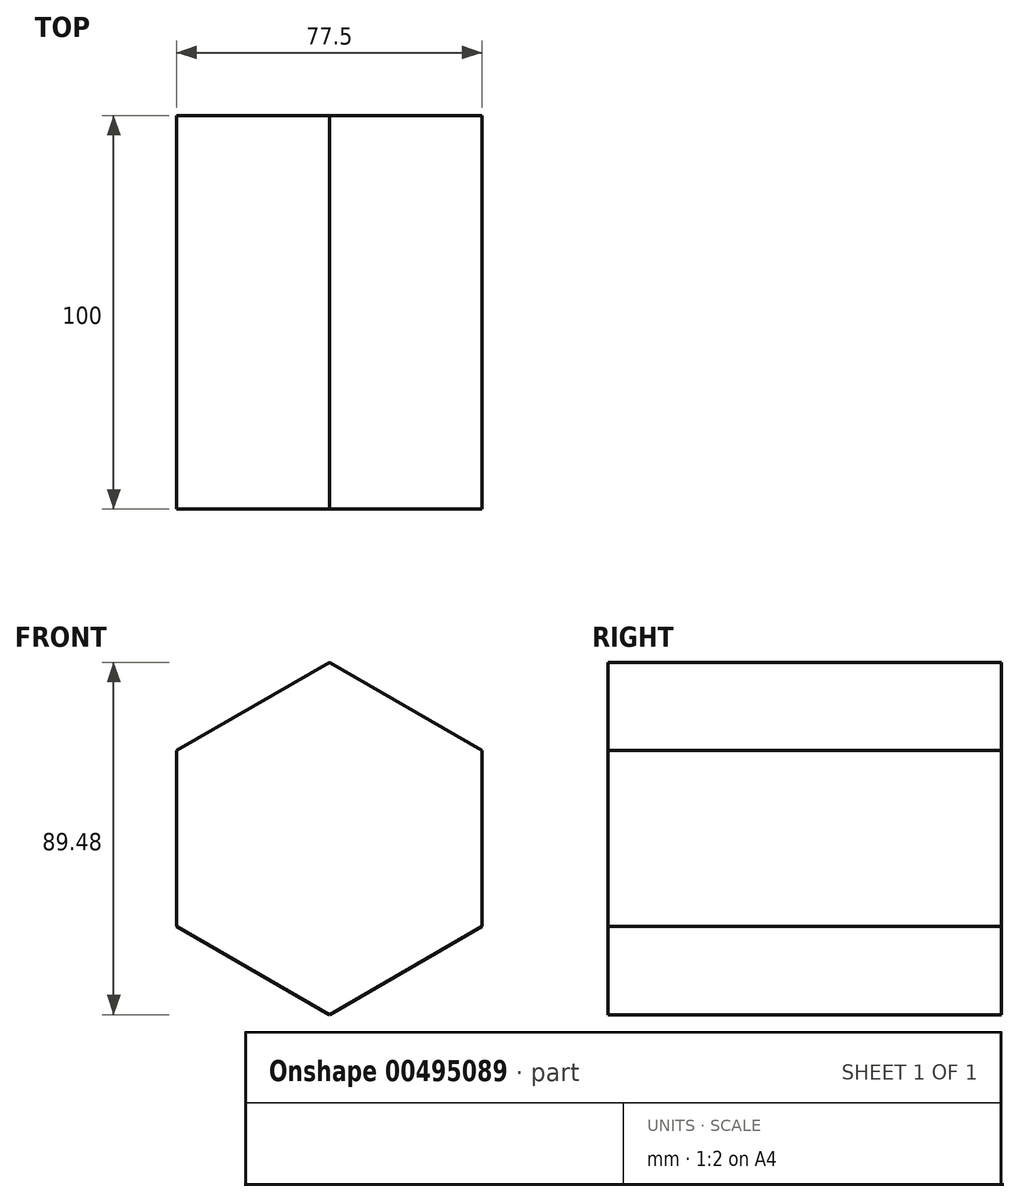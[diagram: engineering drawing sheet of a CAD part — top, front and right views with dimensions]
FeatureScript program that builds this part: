
annotation { "Feature Type Name" : "Feature", "Feature Type Description" : "" }
export const myFeature = defineFeature(function(context is Context, id is Id, definition is map)
    precondition{}
    {
        {
            var Q0;
            Q0=qCreatedBy(makeId("Front.planeOp"),FACE);
            var sketch = newSketch(context, id + "F0", { "sketchPlane" : qUnion([Q0])});
            skCircle(sketch, "E0.cCircle", {"center": v(0, 0) * mm, "radius": 44.74 * mm, "construction": true});
            skLineSegment(sketch, "E0.0", {"start": v(38.75, -22.37) * mm, "end": v(0, -44.74) * mm});
            skLineSegment(sketch, "E0.1", {"start": v(0, -44.74) * mm, "end": v(-38.75, -22.37) * mm});
            skLineSegment(sketch, "E0.2", {"start": v(-38.75, -22.37) * mm, "end": v(-38.75, 22.37) * mm});
            skLineSegment(sketch, "E0.3", {"start": v(-38.75, 22.37) * mm, "end": v(0, 44.74) * mm});
            skLineSegment(sketch, "E0.4", {"start": v(0, 44.74) * mm, "end": v(38.75, 22.37) * mm});
            skLineSegment(sketch, "E0.5", {"start": v(38.75, 22.37) * mm, "end": v(38.75, -22.37) * mm});
            skSolve(sketch);
        }
        {
            var Q0;
            Q0 = qSketchRegion(id + "F0", true);
            extrude(context, id + "F1", {"entities" : qUnion([Q0]), "depth" : 100 * mm});
        }
    });
